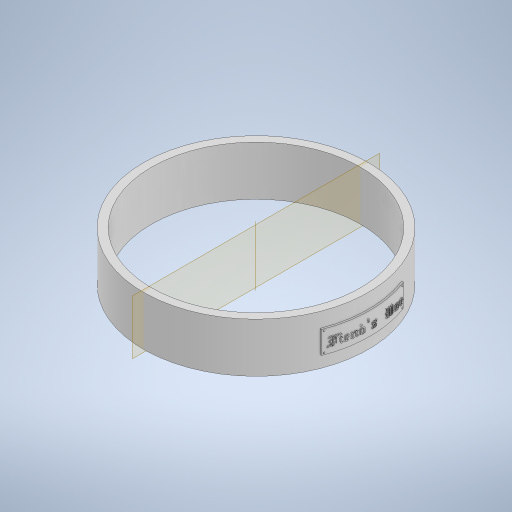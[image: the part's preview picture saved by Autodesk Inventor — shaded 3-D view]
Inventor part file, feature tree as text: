
AUTODESK INVENTOR PART (.ipt)
format: ipt  version: 2023 (Build 270158000, 158)  size: 4,596,224 bytes
history: native  units: in
note: dims shown in document units (in); Inventor stores cm internally (conversion verified against a paired STEP export)
features: emboss x3, pattern_circular x3, other x2, extrude x1, plane x1, fillet x1, sketch x1
ambient origin geometry x8: Origin, YZ Plane, XZ Plane, XY Plane, X Axis, Y Axis, Z Axis, Center Point
bodies: Solid1 (feature_tree)
feature tree (12):
  extrude  "Extrusion1"  Depth=0.3937in
  plane  "Work Plane1"
  other  "Text"
  emboss  "Emboss4"
  emboss  "Emboss5"
  emboss  "Emboss6"
  fillet  "Rivots"  Radius=0.8661in
  pattern_circular  "Circular Pattern1"  Count=6  [1 undecoded]
  pattern_circular  "Circular Pattern2"  [2 undecoded]
  pattern_circular  "Circular Pattern3"  [2 undecoded]
  sketch  "Sketch1"  dims[d0=3.937in d1=3.6614in d2=0.8661in d3=0.0in d4=2.3622in d6=0.4546in d10=0.0in d11=0.3937in d12=1.4567in d19=0.0in d20=0.0in d21=0.0295in d22=0.0in d23=0.0197in d24=0.0in d25=0.0295in d26=0.0295in d27=0.0295in d28=0.0157in d29=0.0in d30=0.0138in d31=0.7874in d32=360.0deg d34=0.7874in d35=360.0deg d37=0.7874in d38=360.0deg d33=0.0in]
  other  "NamePlate"
note: 5 required parameter values undecoded (feature->parameter linkage not recoverable at this tier; creation-order binding heuristic only, values carry confidence <= 0.55)
